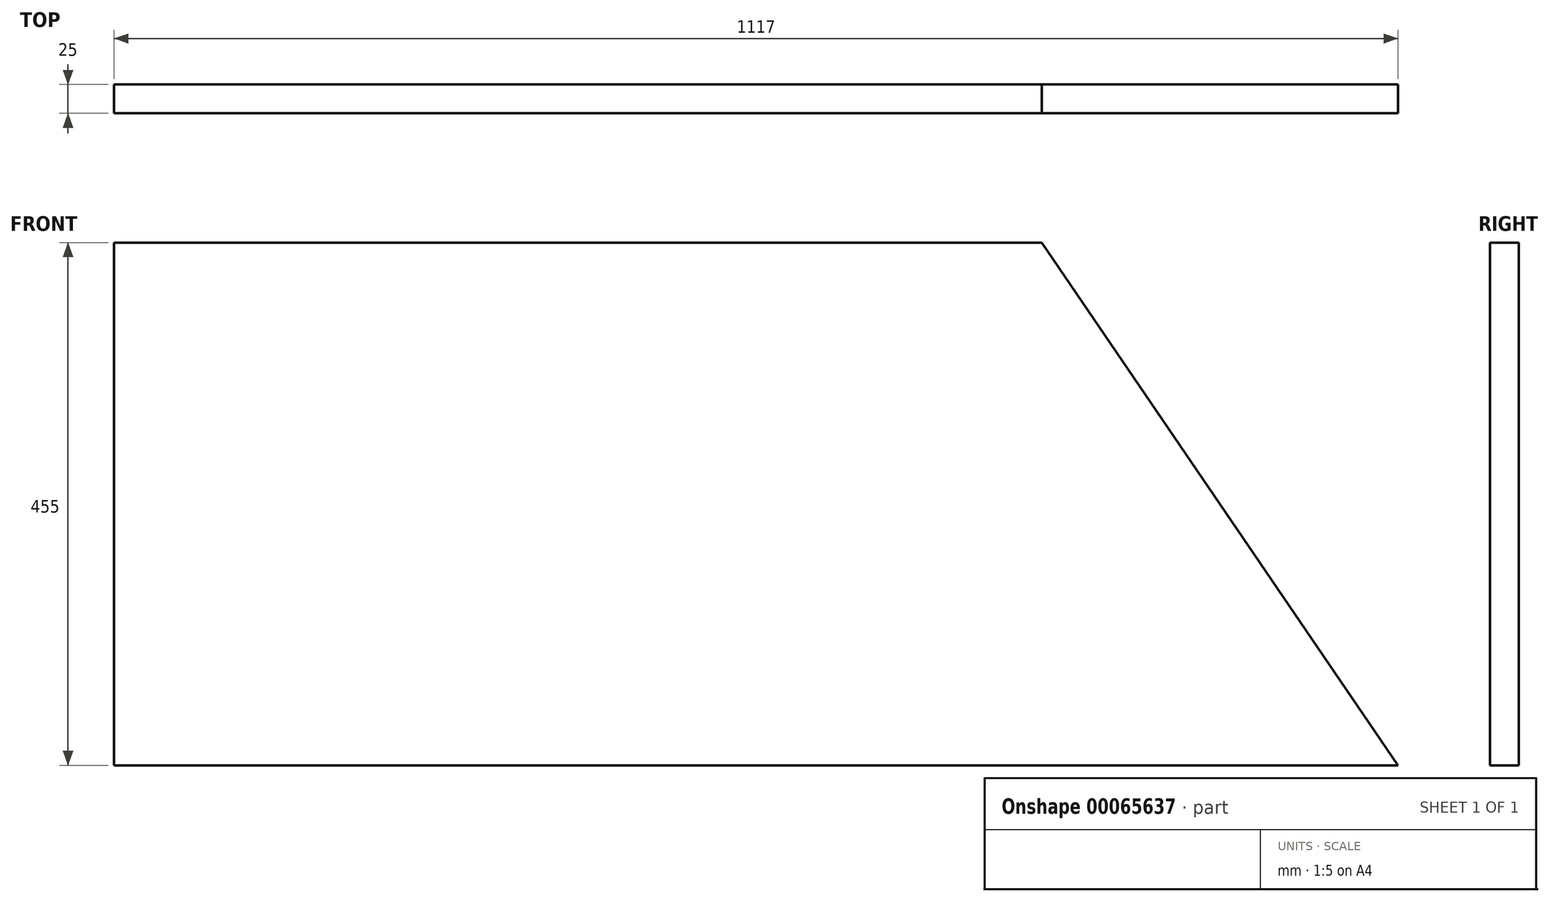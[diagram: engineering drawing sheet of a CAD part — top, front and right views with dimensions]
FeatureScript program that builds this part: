
annotation { "Feature Type Name" : "Feature", "Feature Type Description" : "" }
export const myFeature = defineFeature(function(context is Context, id is Id, definition is map)
    precondition{}
    {
        {
            var Q0;
            Q0=qCreatedBy(makeId("Front.planeOp"),FACE);
            var sketch = newSketch(context, id + "F0", { "sketchPlane" : qUnion([Q0])});
            skLineSegment(sketch, "E0.bottom", {"start": v(0, 0) * mm, "end": v(1117, 0) * mm});
            skLineSegment(sketch, "E0.top", {"start": v(0, 455) * mm, "end": v(807, 455) * mm});
            skLineSegment(sketch, "E0.left", {"start": v(0, 0) * mm, "end": v(0, 455) * mm});
            skLineSegment(sketch, "E0.right", {"start": v(1117, 0) * mm, "end": v(807, 455) * mm});
            skLineSegment(sketch, "E1", {"start": v(225, 0) * mm, "end": v(225, 455) * mm, "construction": true});
            skLineSegment(sketch, "E2", {"start": v(597, 0) * mm, "end": v(597, 455) * mm, "construction": true});
            skSolve(sketch);
        }
        {
            var Q0;
            {var subQ0=sQuery(id+"F0.wireOp",EDGE,"E0.right");Q0=makeQuery(id+"F0.imprint","IMPRINT",FACE,{"disambiguationData":[TD([[makeQuery(id+"F0.imprint","IMPRINT",EDGE,{"derivedFrom":subQ0}),1.0]])]});}
            var Q1;
            {var subQ0=sQuery(id+"F0.wireOp",EDGE,"E1");Q1=makeQuery(id+"F0.imprint","IMPRINT",FACE,{"disambiguationData":[TD([[makeQuery(id+"F0.imprint","IMPRINT",EDGE,{"derivedFrom":subQ0}),-1.0]])]});}
            var Q2;
            {var subQ0=sQuery(id+"F0.wireOp",EDGE,"E0.left");Q2=makeQuery(id+"F0.imprint","IMPRINT",FACE,{"disambiguationData":[TD([[makeQuery(id+"F0.imprint","IMPRINT",EDGE,{"derivedFrom":subQ0}),-1.0]])]});}
            extrude(context, id + "F1", {"entities" : qUnion([Q0, Q1, Q2]), "depth" : 25 * mm});
        }
    });
